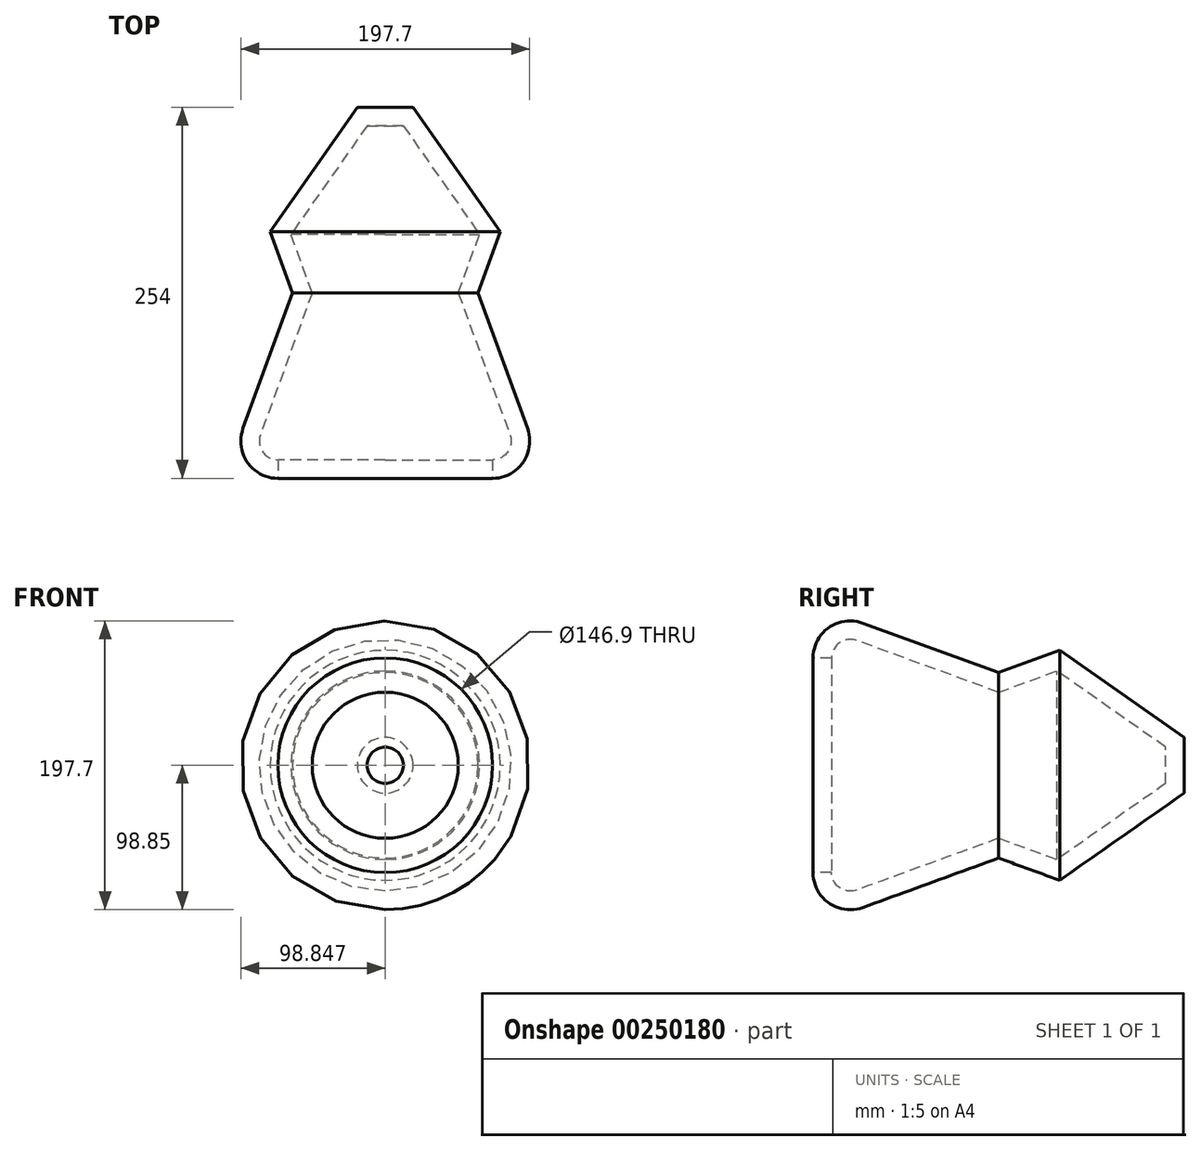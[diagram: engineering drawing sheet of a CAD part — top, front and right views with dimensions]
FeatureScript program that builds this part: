
annotation { "Feature Type Name" : "Feature", "Feature Type Description" : "" }
export const myFeature = defineFeature(function(context is Context, id is Id, definition is map)
    precondition{}
    {
        {
            var Q0;
            Q0=qCreatedBy(makeId("Front.planeOp"),FACE);
            var sketch = newSketch(context, id + "F0", { "sketchPlane" : qUnion([Q0])});
            skCircle(sketch, "E0", {"center": v(1.6, 0) * mm, "radius": 63.5 * mm});
            skSolve(sketch);
        }
        {
            var Q0;
            Q0=makeQuery(id+"F0.imprint","IMPRINT",FACE,{"disambiguationData":[TD([[makeQuery(id+"F0.imprint","IMPRINT",EDGE,{"derivedFrom":sQuery(id+"F0.wireOp",EDGE,"E0")}),1.0]])]});
            extrude(context, id + "F1", {"entities" : qUnion([Q0]), "endBound" : BoundingType.SYMMETRIC, "depth" : 254 * mm, "hasDraft" : true, "draftAngle" : 20 * degree});
        }
        {
            var Q0;
            Q0=makeQuery(id+"F1.opExtrude","CAP_FACE",FACE,{"disambiguationData":[OSD([sQuery(id+"F0.wireOp",EDGE,"E0")])],"isStart":false});
            fillet(context, id + "F2", {"entities" : qUnion([Q0]), "radius" : 25.4 * mm, "tangentPropagation" : true, "allowEdgeOverflow" : false});
        }
        {
            var Q0;
            Q0=makeQuery(id+"F1.opExtrude","CAP_FACE",FACE,{"disambiguationData":[OSD([sQuery(id+"F0.wireOp",EDGE,"E0")])],"isStart":true});
            chamfer(context, id + "F3", {"entities" : qUnion([Q0]), "width" : 63.5 * mm, "tangentPropagation" : true});
        }
        {
            var Q0;
            Q0=makeQuery(id+"F1.opExtrude","CAP_FACE",FACE,{"disambiguationData":[OSD([sQuery(id+"F0.wireOp",EDGE,"E0")])],"isStart":false});
            shell(context, id + "F4", {"entities" : qUnion([Q0]), "thickness" : 12.7 * mm});
        }
    });
